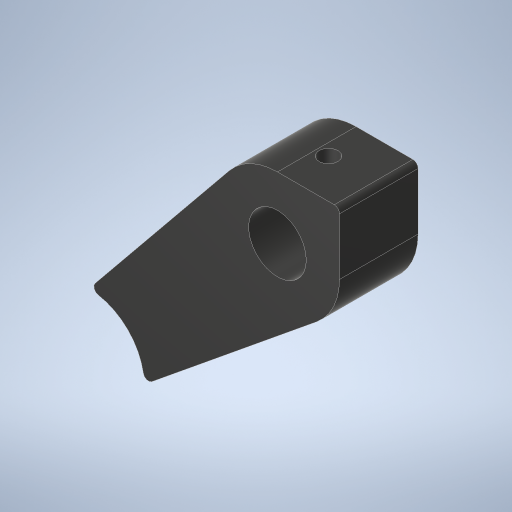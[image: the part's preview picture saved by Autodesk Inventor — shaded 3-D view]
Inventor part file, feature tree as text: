
AUTODESK INVENTOR PART (.ipt)
format: ipt  version: 2023.4 (Build 274418000, 418)  size: 284,160 bytes
history: native  units: in
note: dims shown in document units (in); Inventor stores cm internally (conversion verified against a paired STEP export)
features: sketch x4, extrude x3, fillet x1, mirror x1, plane x1, projected_geometry x1
ambient origin geometry x8: Origin, YZ Plane, XZ Plane, XY Plane, X Axis, Y Axis, Z Axis, Center Point
bodies: Solid1 (feature_tree)
feature tree (11):
  extrude  "Extrusion1"  Depth=6.0in
  fillet  "Fillet1"  Radius=1.32in
  extrude  "Extrusion2"  Depth=1.5in
  mirror  "Mirror1"
  sketch  "Sketch3"  dims[d6=0.0312in d7=0.01in]
  plane  "Work Plane1"
  extrude  "Extrusion3"  Depth=0.01in
  sketch  "Sketch1"  dims[d0=6.0in d1=6.0in d2=1.32in]
  sketch  "Sketch2"  dims[d3=0.6875in d4=1.5in]
  projected_geometry  "Projected Loop1"
  sketch  "Sketch5"  dims[d8=0.01in d9=0.9375in d10=0.0in d11=0.0625in d12=1.125in d13=0.0625in d14=0.0in d15=0.24in d17=1.0in d18=2.25in d19=2.25in d20=45.0deg d28=0.6in d29=0.2264in d30=0.3in d31=0.0in]
